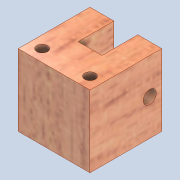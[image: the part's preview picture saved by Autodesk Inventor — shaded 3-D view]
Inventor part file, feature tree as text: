
AUTODESK INVENTOR PART (.ipt)
format: ipt  version: 2020 (Build 240168000, 168)  size: 325,632 bytes
history: native  units: mm
features: sketch x4, extrude x3, hole x1, projected_geometry x1
ambient origin geometry x8: Origin, YZ Plane, XZ Plane, XY Plane, X Axis, Y Axis, Z Axis, Center Point
bodies: Solid1 (feature_tree)
feature tree (9):
  extrude  "Extrusion1"  Depth=30.0mm
  extrude  "Extrusion3"  Depth=10.0mm
  hole  "Hole1"  [1 undecoded]
  extrude  "Extrusion6"  Depth=4.5mm
  sketch  "Sketch1"  dims[d0=30.0mm d1=30.0mm]
  sketch  "Sketch4"  dims[d2=30.0mm d3=0.0mm d8=10.0mm]
  sketch  "Sketch5"  dims[d9=15.0mm d10=0.0mm d11=5.0mm]
  sketch  "Sketch8"  dims[d12=5.5mm d13=6.0mm d14=4.0mm d15=2.0mm d16=90.0deg d17=8.0mm d18=20.594885mm d28=4.5mm d30=5.0mm d31=5.0mm d32=5.0mm d33=0.0mm d34=0.0mm]
  projected_geometry  "Projected Loop1"
note: 1 required parameter value undecoded (feature->parameter linkage not recoverable at this tier; creation-order binding heuristic only, values carry confidence <= 0.55)
